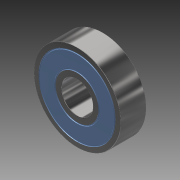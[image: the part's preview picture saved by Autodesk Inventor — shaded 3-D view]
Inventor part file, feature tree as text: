
AUTODESK INVENTOR PART (.ipt)
format: ipt  version: 2014 (Build 180170000, 170)  size: 180,224 bytes
history: native  units: in
note: dims shown in document units (in); Inventor stores cm internally (conversion verified against a paired STEP export)
features: sketch x2, extrude x1, fillet x1, revolve x1, plane x1, mirror x1
ambient origin geometry x8: Origin, YZ Plane, XZ Plane, XY Plane, X Axis, Y Axis, Z Axis, Center Point
bodies: Solid1 (feature_tree)
feature tree (7):
  extrude  "Extrusion1"  Depth=0.5512in
  fillet  "Fillet1"  Radius=0.5512in
  revolve  "Revolution1"  Angle=90.0deg
  plane  "Work Plane1"
  mirror  "Mirror1"
  sketch  "Sketch1"  dims[d0=0.6693in d1=1.8504in d2=0.5512in d3=0.0in]
  sketch  "Sketch2"  dims[d4=0.0118in d5=90.0deg]
